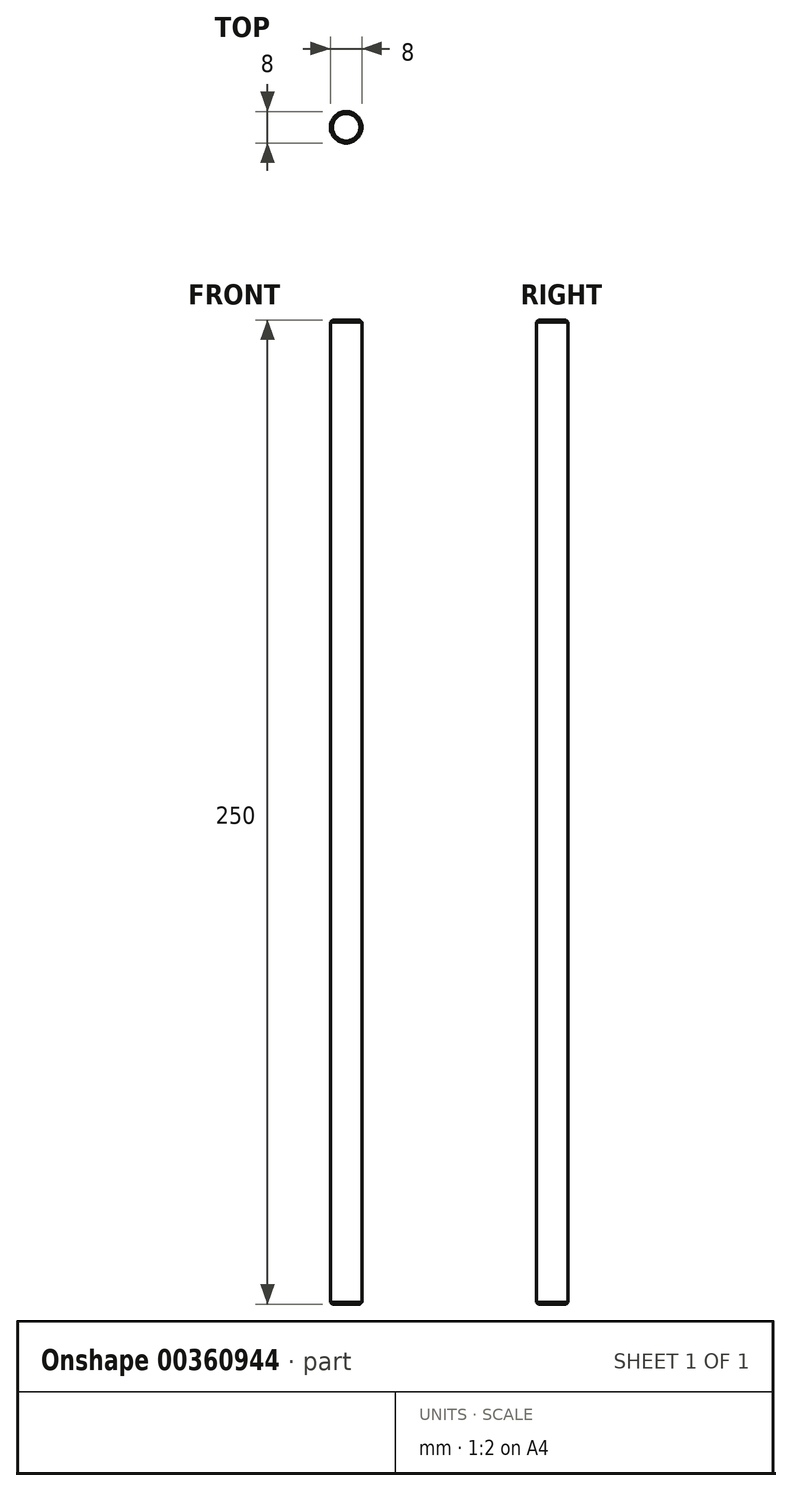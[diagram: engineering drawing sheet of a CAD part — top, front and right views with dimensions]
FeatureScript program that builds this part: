
annotation { "Feature Type Name" : "Feature", "Feature Type Description" : "" }
export const myFeature = defineFeature(function(context is Context, id is Id, definition is map)
    precondition{}
    {
        {
            var Q0;
            Q0=qCreatedBy(makeId("Top.planeOp"),FACE);
            var sketch = newSketch(context, id + "F0", { "sketchPlane" : qUnion([Q0])});
            skCircle(sketch, "E0", {"center": v(0, 0) * mm, "radius": 4 * mm});
            skSolve(sketch);
        }
        {
            var Q0;
            Q0 = qSketchRegion(id + "F0", true);
            extrude(context, id + "F1", {"entities" : qUnion([Q0]), "depth" : 250 * mm});
        }
        {
            var Q0;
            Q0=makeQuery(id+"F1.opExtrude","CAP_FACE",FACE,{"disambiguationData":[OSD([sQuery(id+"F0.wireOp",EDGE,"E0")])],"isStart":false});
            var Q1;
            Q1=makeQuery(id+"F1.opExtrude","CAP_FACE",FACE,{"disambiguationData":[OSD([sQuery(id+"F0.wireOp",EDGE,"E0")])],"isStart":true});
            chamfer(context, id + "F2", {"entities" : qUnion([Q0, Q1]), "width" : 0.5 * mm, "tangentPropagation" : true});
        }
    });
